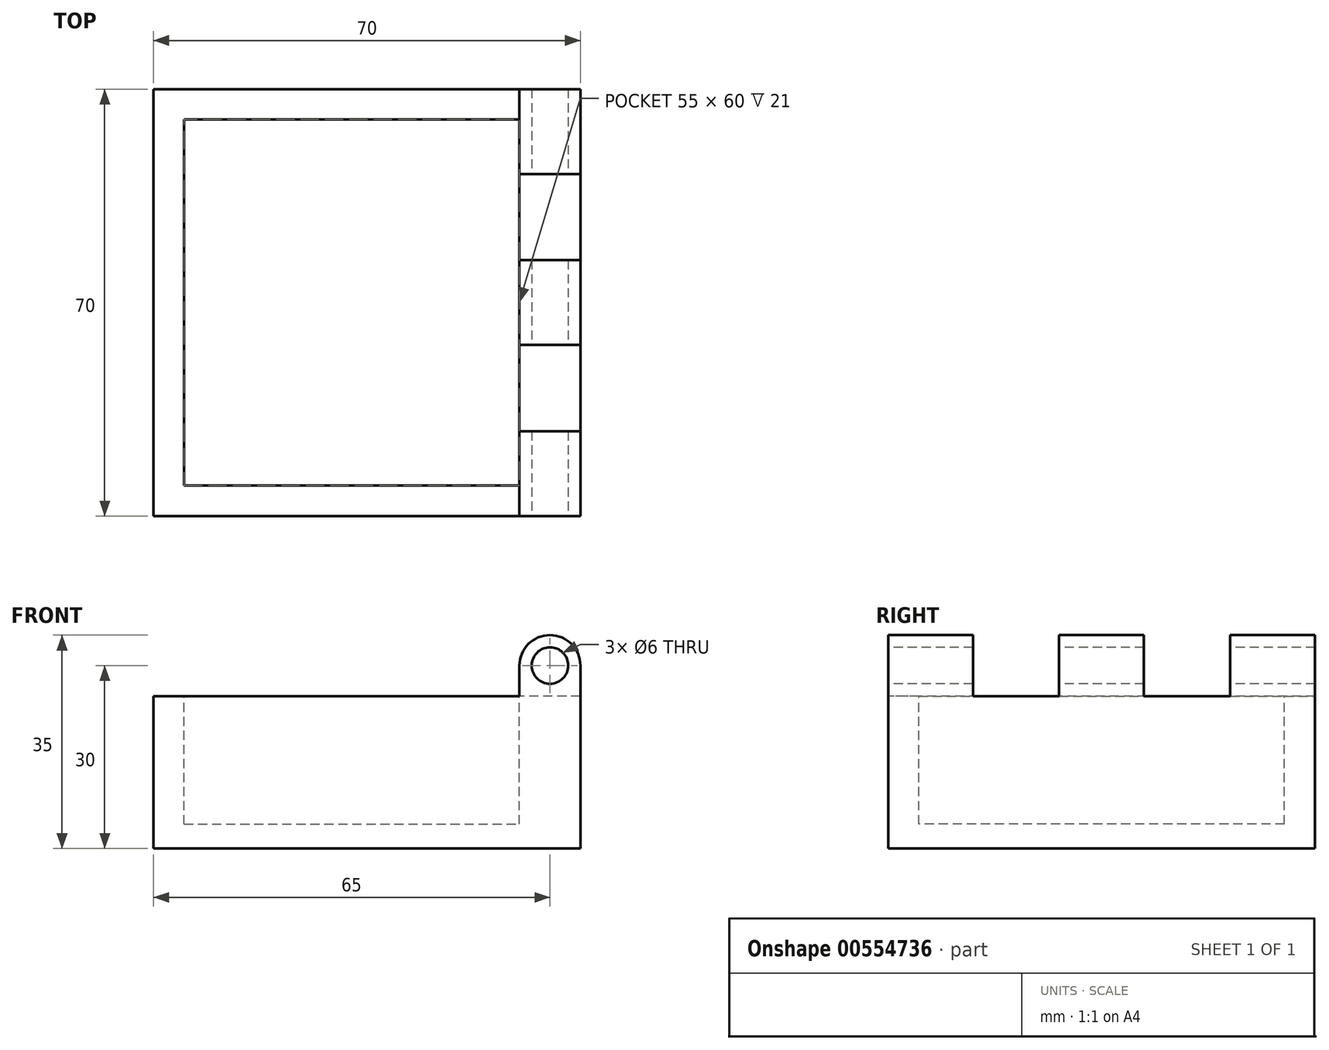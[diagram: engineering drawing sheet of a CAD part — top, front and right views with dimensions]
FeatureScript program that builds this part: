
annotation { "Feature Type Name" : "Feature", "Feature Type Description" : "" }
export const myFeature = defineFeature(function(context is Context, id is Id, definition is map)
    precondition{}
    {
        {
            var Q0;
            Q0=qCreatedBy(makeId("Top.planeOp"),FACE);
            var sketch = newSketch(context, id + "F0", { "sketchPlane" : qUnion([Q0])});
            skLineSegment(sketch, "E0.bottom", {"start": v(25, 25) * mm, "end": v(-25, 25) * mm});
            skLineSegment(sketch, "E0.top", {"start": v(25, -25) * mm, "end": v(-25, -25) * mm});
            skLineSegment(sketch, "E0.left", {"start": v(25, 25) * mm, "end": v(25, -25) * mm});
            skLineSegment(sketch, "E0.right", {"start": v(-25, 25) * mm, "end": v(-25, -25) * mm});
            skPoint(sketch, "E0.middle", {"position": v(0, 0) * mm});
            skLineSegment(sketch, "E1.0", {"start": v(35, 35) * mm, "end": v(-35, 35) * mm});
            skLineSegment(sketch, "E1.1", {"start": v(35, 35) * mm, "end": v(35, -35) * mm});
            skLineSegment(sketch, "E1.2", {"start": v(35, -35) * mm, "end": v(-35, -35) * mm});
            skLineSegment(sketch, "E1.3", {"start": v(-35, 35) * mm, "end": v(-35, -35) * mm});
            skSolve(sketch);
        }
        {
            var Q0;
            Q0=makeQuery(id+"F0.imprint","IMPRINT",FACE,{"disambiguationData":[TD([[makeQuery(id+"F0.imprint","IMPRINT",EDGE,{"derivedFrom":sQuery(id+"F0.wireOp",EDGE,"E0.bottom")}),1.0]])]});
            extrude(context, id + "F1", {"entities" : qUnion([Q0]), "depth" : 4 * mm, "offsetDistance" : 25 * mm});
        }
        {
            var Q0;
            Q0=makeQuery(id+"F0.imprint","IMPRINT",FACE,{"disambiguationData":[TD([[makeQuery(id+"F0.imprint","IMPRINT",EDGE,{"derivedFrom":sQuery(id+"F0.wireOp",EDGE,"E0.bottom")}),-1.0]])]});
            extrude(context, id + "F2", {"entities" : qUnion([Q0]), "operationType" : NewBodyOperationType.ADD, "depth" : 25 * mm, "offsetDistance" : 25 * mm});
        }
        {
            var Q0;
            Q0=makeQuery(id+"F2.opExtrude","CAP_FACE",FACE,{"disambiguationData":[OSD([sQuery(id+"F0.wireOp",EDGE,"E0.bottom"),sQuery(id+"F0.wireOp",EDGE,"E0.top"),sQuery(id+"F0.wireOp",EDGE,"E0.left"),sQuery(id+"F0.wireOp",EDGE,"E0.right"),sQuery(id+"F0.wireOp",EDGE,"E1.0"),sQuery(id+"F0.wireOp",EDGE,"E1.1"),sQuery(id+"F0.wireOp",EDGE,"E1.2"),sQuery(id+"F0.wireOp",EDGE,"E1.3")])],"isStart":false});
            var sketch = newSketch(context, id + "F3", { "sketchPlane" : qUnion([Q0])});
            skLineSegment(sketch, "E2", {"start": v(35, -21.1) * mm, "end": v(25, -21.1) * mm});
            skLineSegment(sketch, "E3", {"start": v(35, 21.1) * mm, "end": v(25, 21.1) * mm});
            skLineSegment(sketch, "E4", {"start": v(25, -21.1) * mm, "end": v(25, -35) * mm});
            skLineSegment(sketch, "E5", {"start": v(25, -7) * mm, "end": v(25, -6.95) * mm});
            skLineSegment(sketch, "E6", {"start": v(25, 21.1) * mm, "end": v(25, 35) * mm});
            skLineSegment(sketch, "E7", {"start": v(25, -6.95) * mm, "end": v(25, 6.95) * mm});
            skLineSegment(sketch, "E8", {"start": v(25, -6.95) * mm, "end": v(35, -6.95) * mm});
            skLineSegment(sketch, "E9", {"start": v(25, 6.95) * mm, "end": v(35, 6.95) * mm});
            skSolve(sketch);
        }
        {
            var Q0;
            {var subQ3=sQuery(id+"F3.wireOp",EDGE,"E2");Q0=makeQuery(id+"F3.imprint","IMPRINT",FACE,{"disambiguationData":[TD([[makeQuery(id+"F3.imprint","IMPRINT",EDGE,{"derivedFrom":subQ3}),1.0]])]});}
            var Q1;
            {var subQ0=sQuery(id+"F3.wireOp",EDGE,"o40LY4OS-RRcS-k7l7-HTMt-9sDN2KFWIE5B");Q1=makeQuery(id+"F3.imprint","IMPRINT",FACE,{"disambiguationData":[TD([[makeQuery(id+"F3.imprint","IMPRINT",EDGE,{"derivedFrom":subQ0}),-1.0]])]});}
            var Q2;
            {var subQ6=sQuery(id+"F3.wireOp",EDGE,"E3");Q2=makeQuery(id+"F3.imprint","IMPRINT",FACE,{"disambiguationData":[TD([[makeQuery(id+"F3.imprint","IMPRINT",EDGE,{"derivedFrom":subQ6}),-1.0]])]});}
            var Q3;
            Q3=makeQuery(id+"F3.imprint","IMPRINT",FACE,{"disambiguationData":[TD([[makeQuery(id+"F3.imprint","IMPRINT",EDGE,{"derivedFrom":sQuery(id+"F3.wireOp",EDGE,"E7")}),1.0]])]});
            extrude(context, id + "F4", {"entities" : qUnion([Q0, Q1, Q2, Q3]), "operationType" : NewBodyOperationType.ADD, "depth" : 10 * mm, "offsetDistance" : 25 * mm});
        }
        {
            var Q0;
            Q0=makeQuery(id+"F4.opExtrude","SWEPT_FACE",FACE,{"disambiguationData":[OSD([sQuery(id+"F0.wireOp",EDGE,"E1.2")])]});
            var sketch = newSketch(context, id + "F5", { "sketchPlane" : qUnion([Q0])});
            skPoint(sketch, "E10.endSnap0", {"position": v(30, 35) * mm});
            skCircle(sketch, "E11", {"center": v(30, 30) * mm, "radius": 3 * mm});
            skPoint(sketch, "E10.start.orphan", {"position": v(35, 17.5) * mm});
            skLineSegment(sketch, "E12", {"start": v(35, 35) * mm, "end": v(35, 30) * mm});
            skArc(sketch, "E13", {"start": v(35, 30) * mm, "mid": v(33.54, 33.54) * mm, "end": v(30, 35) * mm});
            skLineSegment(sketch, "E14", {"start": v(25, 25) * mm, "end": v(25.05, 25) * mm});
            skPoint(sketch, "E15.orphan", {"position": v(25, 30) * mm});
            skArc(sketch, "E16", {"start": v(30, 35) * mm, "mid": v(26.46, 33.54) * mm, "end": v(25, 30) * mm});
            skSolve(sketch);
        }
        {
            var Q0;
            Q0=makeQuery(id+"F5.imprint","IMPRINT",FACE,{"disambiguationData":[TD([[makeQuery(id+"F5.imprint","IMPRINT",EDGE,{"derivedFrom":sQuery(id+"F5.wireOp",EDGE,"E11")}),1.0]])]});
            var Q1;
            {var subQ0=sQuery(id+"F5.wireOp",EDGE,"E12");Q1=makeQuery(id+"F5.imprint","IMPRINT",FACE,{"disambiguationData":[TD([[makeQuery(id+"F5.imprint","IMPRINT",EDGE,{"derivedFrom":subQ0}),-1.0]])]});}
            var Q2;
            {var subQ0=sQuery(id+"F5.wireOp",EDGE,"85n3K37o-f25W-N80d-Xazs-DXxDs474Me9g");Q2=makeQuery(id+"F5.imprint","IMPRINT",FACE,{"disambiguationData":[TD([[makeQuery(id+"F5.imprint","IMPRINT",EDGE,{"derivedFrom":subQ0}),-1.0]])]});}
            var Q3;
            {var subQ5=sQuery(id+"F5.wireOp",EDGE,"E14");Q3=makeQuery(id+"F5.imprint","IMPRINT",FACE,{"disambiguationData":[TD([[makeQuery(id+"F5.imprint","IMPRINT",EDGE,{"derivedFrom":subQ5}),1.0]])]});}
            var Q4;
            {var subQ0=sQuery(id+"F5.wireOp",EDGE,"E16");Q4=makeQuery(id+"F5.imprint","IMPRINT",FACE,{"disambiguationData":[TD([[makeQuery(id+"F5.imprint","IMPRINT",EDGE,{"derivedFrom":subQ0}),-1.0]])]});}
            extrude(context, id + "F6", {"entities" : qUnion([Q0, Q1, Q2, Q3, Q4]), "operationType" : NewBodyOperationType.REMOVE, "endBound" : BoundingType.THROUGH_ALL, "oppositeDirection" : true, "depth" : 14 * mm, "offsetDistance" : 25 * mm});
        }
        {
            var Q0;
            {var subQ0=sQuery(id+"F0.wireOp",EDGE,"E1.3");var subQ1=sQuery(id+"F0.wireOp",EDGE,"E1.2");var subQ2=sQuery(id+"F0.wireOp",EDGE,"E1.0");var subQ3=sQuery(id+"F0.wireOp",EDGE,"E0.bottom");var subQ4=sQuery(id+"F0.wireOp",EDGE,"E0.right");var subQ5=sQuery(id+"F0.wireOp",EDGE,"E0.top");var subQ6=sQuery(id+"F0.wireOp",EDGE,"E0.left");Q0=makeQuery(id+"F4.boolean.opBoolean","SPLIT",FACE,{"disambiguationData":[TD([makeQuery(id+"F2.opExtrude","SWEPT_FACE",FACE,{"disambiguationData":[OSD([subQ3])]})])],"derivedFrom":makeQuery(id+"F2.opExtrude","CAP_FACE",FACE,{"disambiguationData":[OSD([subQ3,subQ5,subQ6,subQ4,subQ2,sQuery(id+"F0.wireOp",EDGE,"E1.1"),subQ1,subQ0])],"isStart":false})});}
            var sketch = newSketch(context, id + "F7", { "sketchPlane" : qUnion([Q0])});
            skLineSegment(sketch, "E17", {"start": v(25, -30) * mm, "end": v(-30, -30) * mm});
            skLineSegment(sketch, "E18", {"start": v(-30, -30) * mm, "end": v(-30, 30) * mm});
            skPoint(sketch, "E18.endSnap0", {"position": v(25, 30) * mm});
            skLineSegment(sketch, "E19", {"start": v(-30, 30) * mm, "end": v(25, 30) * mm});
            skSolve(sketch);
        }
        {
            var Q0;
            {var subQ2=sQuery(id+"F7.wireOp",EDGE,"E17");Q0=makeQuery(id+"F7.imprint","IMPRINT",FACE,{"disambiguationData":[TD([[makeQuery(id+"F7.imprint","IMPRINT",EDGE,{"derivedFrom":subQ2}),-1.0]])]});}
            extrude(context, id + "F8", {"entities" : qUnion([Q0]), "operationType" : NewBodyOperationType.REMOVE, "oppositeDirection" : true, "depth" : 21 * mm, "offsetDistance" : 25 * mm});
        }
    });
